# Revit family: IS_Ceraplus_A6151_BIM_DE
name_source: partatom
category: Plumbing Fixtures
revit_build: Autodesk Revit MEP 2015 (Build: 20140606_1530(x64)
units: mm (PartAtom-declared; Revit-internal decimal feet)

## types (1)
- A6151AA - IS Sensor-Wand-WT-Arm.UP CERAPLUS, BS2, Temp.über Griff,Batt., Ausl.230mm, Chrom
    Assembly Code = C1030204
    BIMobject category = Basins
    BOSUseNativeGeometries = 1
    Brand url = http://www.idealstandard.co.uk
    Description = A6151AA CERAPLUS build-in sensor shower mounted spout
    EAN code = https://4015413332675
    Edition number = 1
    FaucetFunction = mixed
    FaucetOperation = leverhandle
    FaucetType = pillar
    FlushRate = 0 CF
    FlushingRate = 0
    IFC Classification = Valve
    IfcExportAs = IfcValveType
    IfcExportType = BRASSWARE BASIN
    Installation instructions = http://www.idealspec.co.uk
    Manufacturer name = Ideal Standard
    ManufacturerURL = www.idealstandard.com
    Material = Brass
    Material main = Brassware
    Model = A6151AA
    ModelNumber = A6151AA
    NBS Reference Code = 75-70-52-96
    NBS Reference Description = Water Supply Systems Control Systems
    Name = CERAPLUS build-in sensor shower mounted spout
    NettWeight = 2,45 kg
    Nominal height = 171
    Nominal width = 170
    NominalDepth = 0' - 0"
    NominalHeight = 0' - 6 23/32"
    NominalLength = 0' - 0"
    NominalWidth = 0' - 6 11/16"
    OmniClass Code = 23.45.55.20
    OmniClass Description = Mixing Faucets
    Product Guid = 44cf6e6e-2e91-42e7-80f7-0ccce9aa3b4f
    Product SKU = A6151
    Product data url = https://bimobject.com
    Product family = Sanitary
    Product group = Washbasin taps
    Product name = Ceraplus Basin Thermostatic Electronic Spout/230 Kit2 Battery
    Product url = www.idealstandard.de/produkte
    ProductInformation = www.idealstandard.de/produkte
    QR code = http://bimobject.com
    Shape = Sculptured
    Space = Internal
    SpareParts = www.idealstandard.de/ersatzteile
    Technical description = www.idealstandard.de/produkte
    URL = www.idealstandard.com
    Uniclass 2.0 Code = SS-75-70-52-96
    Uniclass 2.0 Description = Water Supply Systems Control Systems
    Uniclass 2015 Code = Pr_40_20_87_96
    Uniclass 2015 Name = Washbasin manual water supply sets
    ValveOperation = lever
    Version = 1
    VolumeUnits = Litres
    WarrantyDurationParts = 5
    WarrantyDurationUnit = year
    Weight Net (Kg) = 2.45
    WorkingPressure = 1-5 Bar

## geometry (parser evidence)
native form markers: Blend x4, Sweep x1
no freeform markers — native parametric forms only
